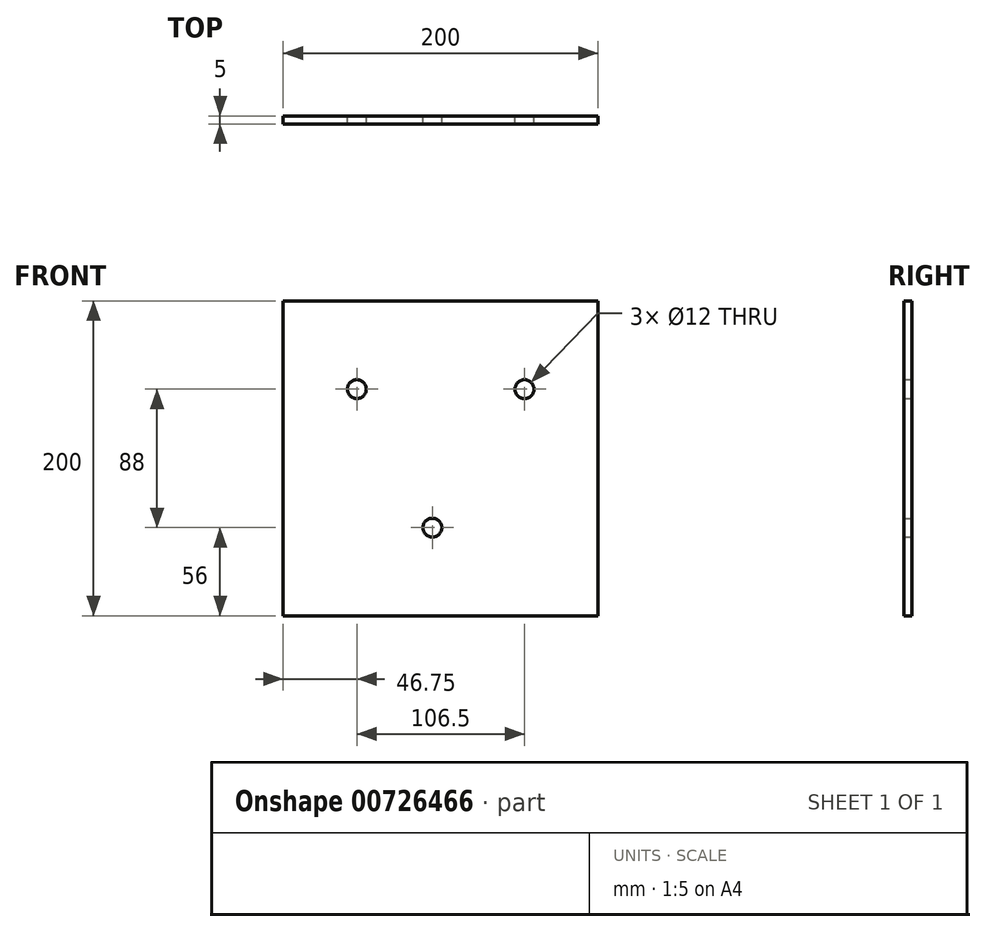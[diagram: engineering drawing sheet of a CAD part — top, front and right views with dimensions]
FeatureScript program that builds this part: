
annotation { "Feature Type Name" : "Feature", "Feature Type Description" : "" }
export const myFeature = defineFeature(function(context is Context, id is Id, definition is map)
    precondition{}
    {
        {
            var Q0;
            Q0=qCreatedBy(makeId("Front.planeOp"),FACE);
            var sketch = newSketch(context, id + "F0", { "sketchPlane" : qUnion([Q0])});
            skLineSegment(sketch, "E0.bottom", {"start": v(0, 0) * mm, "end": v(200, 0) * mm});
            skLineSegment(sketch, "E0.top", {"start": v(0, 200) * mm, "end": v(200, 200) * mm});
            skLineSegment(sketch, "E0.left", {"start": v(0, 0) * mm, "end": v(0, 200) * mm});
            skLineSegment(sketch, "E0.right", {"start": v(200, 0) * mm, "end": v(200, 200) * mm});
            skCircle(sketch, "E1", {"center": v(46.75, 144) * mm, "radius": 6 * mm});
            skCircle(sketch, "E2", {"center": v(153.25, 144) * mm, "radius": 6 * mm});
            skCircle(sketch, "E3", {"center": v(94.75, 56) * mm, "radius": 6 * mm});
            skSolve(sketch);
        }
        {
            var Q0;
            Q0=makeQuery(id+"F0.imprint","IMPRINT",FACE,{"disambiguationData":[TD([[makeQuery(id+"F0.imprint","IMPRINT",EDGE,{"derivedFrom":sQuery(id+"F0.wireOp",EDGE,"E0.bottom")}),1.0]])]});
            extrude(context, id + "F1", {"entities" : qUnion([Q0]), "depth" : 5 * mm, "offsetDistance" : 25 * mm});
        }
    });
